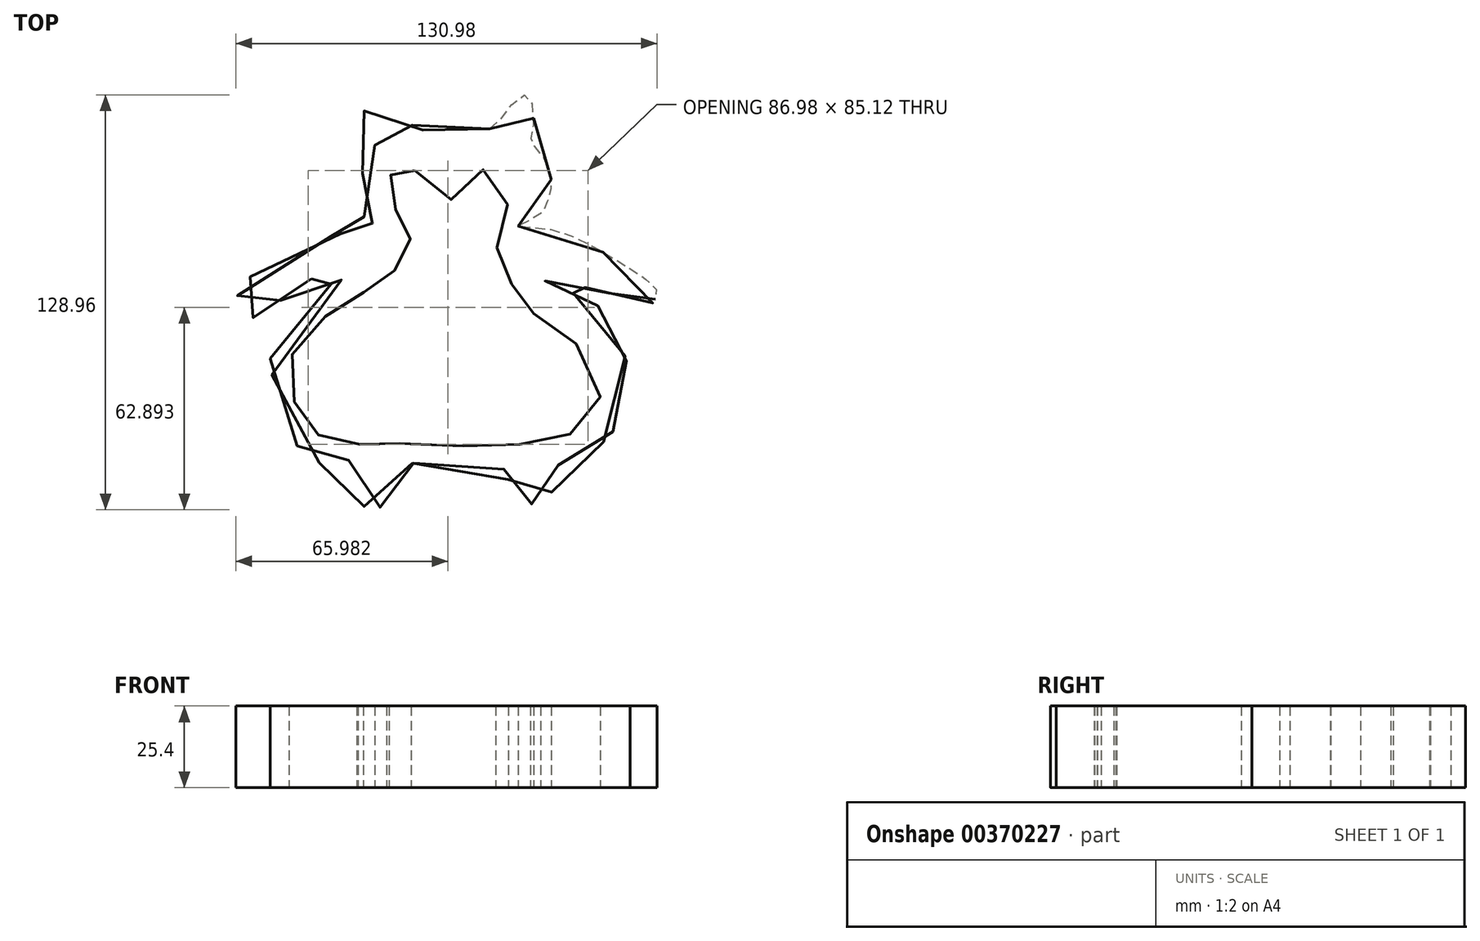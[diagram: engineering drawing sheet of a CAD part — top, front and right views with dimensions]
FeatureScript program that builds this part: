
annotation { "Feature Type Name" : "Feature", "Feature Type Description" : "" }
export const myFeature = defineFeature(function(context is Context, id is Id, definition is map)
    precondition{}
    {
        {
            var Q0;
            Q0=qCreatedBy(makeId("Top.planeOp"),FACE);
            var sketch = newSketch(context, id + "F0", { "sketchPlane" : qUnion([Q0])});
            skFitSpline(sketch, "E0", {"points": [v(12.2, 58.67) * mm, v(17.98, 64.77) * mm, v(24.08, 69.04) * mm, v(25.6, 58.37) * mm, v(25, 54.71) * mm, v(28.04, 51.05) * mm, v(31.4, 42.21) * mm, v(30.18, 36.12) * mm, v(27.74, 31.85) * mm, v(21.03, 28.5) * mm, v(27.74, 27.89) * mm, v(40.84, 23.93) * mm, v(55.47, 15.4) * mm, v(64, 8.69) * mm, v(63.7, 5.64) * mm, v(60.35, 2.9) * mm, v(53.04, 5.94) * mm, v(43.59, 9) * mm, v(32.61, 10.82) * mm, v(28.04, 11.43) * mm, v(42.06, 5.94) * mm, v(49.07, 0) * mm, v(53.34, -9) * mm, v(55.78, -22.4) * mm, v(50.9, -34.9) * mm, v(42.06, -42.21) * mm, v(33.53, -45.87) * mm, v(31.4, -54.4) * mm, v(27.13, -57.45) * mm, v(23.16, -57.76) * mm, v(18.29, -52.88) * mm, v(17.07, -47.4) * mm, v(0, -46.18) * mm, v(-16.46, -46.48) * mm, v(-17.98, -55.02) * mm, v(-26.21, -59.28) * mm, v(-30.18, -46.18) * mm, v(-33.53, -44.04) * mm, v(-41.76, -44.96) * mm, v(-49.68, -36.12) * mm, v(-55.78, -15.4) * mm, v(-49.38, 3.81) * mm, v(-28.65, 14.17) * mm, v(-45.11, 11.13) * mm, v(-58.22, 0) * mm, v(-61.57, 0) * mm, v(-66.45, 3.5) * mm, v(-64.62, 9.6) * mm, v(-52.43, 19.96) * mm, v(-24.38, 27.28) * mm, v(-19.81, 27.28) * mm, v(-25, 29.72) * mm, v(-28.65, 35.5) * mm, v(-28.04, 43.43) * mm, v(-23.47, 53.5) * mm, v(-26.82, 64.16) * mm, v(-14.33, 61.42) * mm, v(-9.14, 58.37) * mm, v(0, 58.37) * mm, v(12.2, 58.67) * mm]});
            skFitSpline(sketch, "E1", {"points": [v(-11, 45.71) * mm, v(0, 36.58) * mm, v(9.04, 45.71) * mm, v(17.88, 38.64) * mm, v(14.05, 24.2) * mm, v(17.58, 15.95) * mm, v(20.53, 5.93) * mm, v(28.04, 0) * mm, v(42.93, -12.93) * mm, v(44.7, -31.5) * mm, v(28.04, -38.28) * mm, v(13.75, -40.04) * mm, v(-13.95, -39.16) * mm, v(-24.38, -39.46) * mm, v(-37.23, -38.28) * mm, v(-44.6, -32.97) * mm, v(-49.9, -21.18) * mm, v(-46.66, -6.45) * mm, v(-33.22, 3.81) * mm, v(-24.38, 9.6) * mm, v(-17.07, 14.78) * mm, v(-12.2, 21.8) * mm, v(-15.54, 30.94) * mm, v(-17.37, 34.6) * mm, v(-18.9, 43.43) * mm, v(-15.54, 46.48) * mm, v(-11, 45.71) * mm]});
            skSolve(sketch);
        }
        {
            var Q0;
            Q0 = qSketchRegion(id + "F0", true);
            extrude(context, id + "F1", {"entities" : qUnion([Q0]), "depth" : 25.4 * mm});
        }
    });
